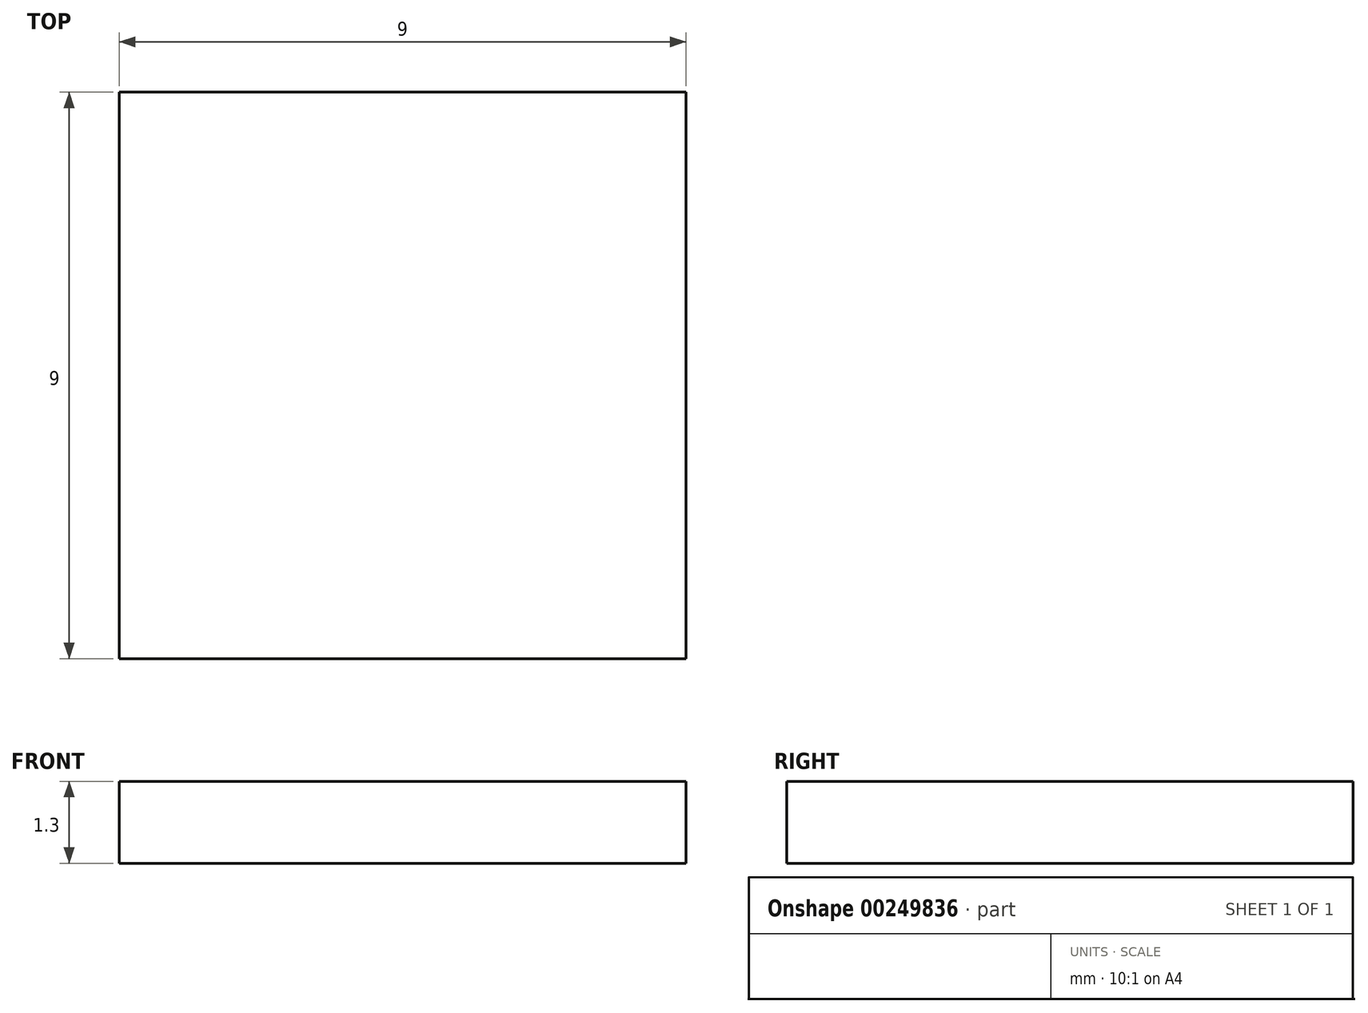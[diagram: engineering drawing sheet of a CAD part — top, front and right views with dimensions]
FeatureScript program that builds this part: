
annotation { "Feature Type Name" : "Feature", "Feature Type Description" : "" }
export const myFeature = defineFeature(function(context is Context, id is Id, definition is map)
    precondition{}
    {
        {
            var Q0;
            Q0=qCreatedBy(makeId("Top.planeOp"),FACE);
            var sketch = newSketch(context, id + "F0", { "sketchPlane" : qUnion([Q0])});
            skLineSegment(sketch, "E0.bottom", {"start": v(0, 0) * mm, "end": v(9, 0) * mm});
            skLineSegment(sketch, "E0.top", {"start": v(0, 9) * mm, "end": v(9, 9) * mm});
            skLineSegment(sketch, "E0.left", {"start": v(0, 0) * mm, "end": v(0, 9) * mm});
            skLineSegment(sketch, "E0.right", {"start": v(9, 0) * mm, "end": v(9, 9) * mm});
            skSolve(sketch);
        }
        {
            var Q0;
            Q0 = qSketchRegion(id + "F0", true);
            extrude(context, id + "F1", {"entities" : qUnion([Q0]), "depth" : 1.3 * mm});
        }
    });
